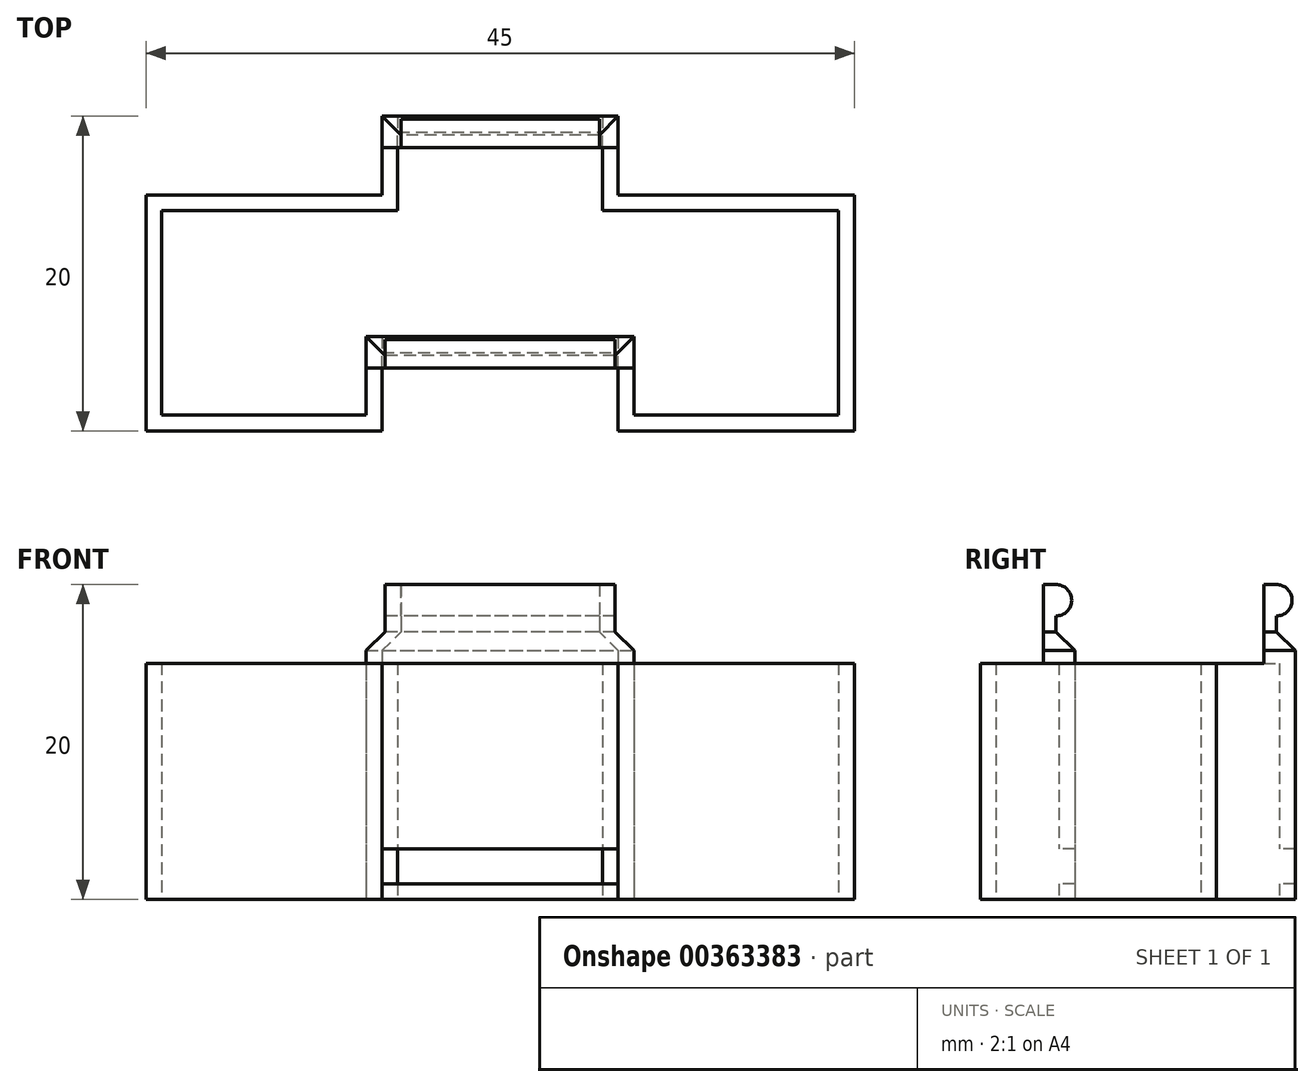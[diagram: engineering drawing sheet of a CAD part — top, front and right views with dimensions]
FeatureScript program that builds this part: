
annotation { "Feature Type Name" : "Feature", "Feature Type Description" : "" }
export const myFeature = defineFeature(function(context is Context, id is Id, definition is map)
    precondition{}
    {
        {
            assignVariable(context, id + "F0", {"name" : "Size", "anyValue" : 15});
        }
        {
            assignVariable(context, id + "F1", {"name" : "Thickness", "anyValue" : 1});
        }
        {
            var Q0;
            Q0=qCreatedBy(makeId("Top.planeOp"),FACE);
            var sketch = newSketch(context, id + "F2", { "sketchPlane" : qUnion([Q0])});
            skLineSegment(sketch, "E0.bottom", {"start": v(-24.33, 0) * mm, "end": v(-39.33, 0) * mm});
            skLineSegment(sketch, "E0.top", {"start": v(-24.33, 15) * mm, "end": v(-39.33, 15) * mm});
            skLineSegment(sketch, "E0.left", {"start": v(-24.33, 0) * mm, "end": v(-24.33, 15) * mm});
            skLineSegment(sketch, "E0.right", {"start": v(-39.33, 0) * mm, "end": v(-39.33, 15) * mm});
            skLineSegment(sketch, "E1.bottom", {"start": v(-9.33, 0) * mm, "end": v(5.67, 0) * mm});
            skLineSegment(sketch, "E1.top", {"start": v(-9.33, 15) * mm, "end": v(5.67, 15) * mm});
            skLineSegment(sketch, "E1.left", {"start": v(-9.33, 0) * mm, "end": v(-9.33, 15) * mm});
            skLineSegment(sketch, "E1.right", {"start": v(5.67, 0) * mm, "end": v(5.67, 15) * mm});
            skLineSegment(sketch, "E2.0", {"start": v(-38.33, 1) * mm, "end": v(-38.33, 14) * mm});
            skLineSegment(sketch, "E2.1", {"start": v(-25.33, 1) * mm, "end": v(-38.33, 1) * mm});
            skLineSegment(sketch, "E2.2", {"start": v(-25.33, 1) * mm, "end": v(-25.33, 14) * mm});
            skLineSegment(sketch, "E2.3", {"start": v(-25.33, 14) * mm, "end": v(-38.33, 14) * mm});
            skLineSegment(sketch, "E3.0", {"start": v(-8.33, 1) * mm, "end": v(-8.33, 14) * mm});
            skLineSegment(sketch, "E3.1", {"start": v(-8.33, 1) * mm, "end": v(4.67, 1) * mm});
            skLineSegment(sketch, "E3.2", {"start": v(4.67, 1) * mm, "end": v(4.67, 14) * mm});
            skLineSegment(sketch, "E3.3", {"start": v(-8.33, 14) * mm, "end": v(4.67, 14) * mm});
            skPoint(sketch, "E4.oppositeSnap0", {"position": v(-9.33, 7.5) * mm});
            skLineSegment(sketch, "E4.bottom", {"start": v(-24.33, 5) * mm, "end": v(-9.33, 5) * mm});
            skLineSegment(sketch, "E4.top", {"start": v(-24.33, 20) * mm, "end": v(-9.33, 20) * mm});
            skLineSegment(sketch, "E4.left", {"start": v(-24.33, 5) * mm, "end": v(-24.33, 20) * mm});
            skLineSegment(sketch, "E4.right", {"start": v(-9.33, 5) * mm, "end": v(-9.33, 20) * mm});
            skLineSegment(sketch, "E5.0", {"start": v(-23.33, 6) * mm, "end": v(-23.33, 19) * mm});
            skLineSegment(sketch, "E5.1", {"start": v(-23.33, 6) * mm, "end": v(-10.33, 6) * mm});
            skLineSegment(sketch, "E5.2", {"start": v(-10.33, 6) * mm, "end": v(-10.33, 19) * mm});
            skLineSegment(sketch, "E5.3", {"start": v(-23.33, 19) * mm, "end": v(-10.33, 19) * mm});
            skLineSegment(sketch, "E6", {"start": v(-25.33, 6) * mm, "end": v(-8.33, 6) * mm});
            skLineSegment(sketch, "E7", {"start": v(-25.33, 14) * mm, "end": v(-8.33, 14) * mm});
            skSolve(sketch);
        }
        {
            var Q0;
            Q0=makeQuery(id+"F2.imprint","IMPRINT",FACE,{"disambiguationData":[TD([[makeQuery(id+"F2.imprint","IMPRINT",EDGE,{"derivedFrom":sQuery(id+"F2.wireOp",EDGE,"E0.bottom")}),-1.0]])]});
            var Q1;
            {var subQ5=sQuery(id+"F2.wireOp",EDGE,"E4.bottom");Q1=makeQuery(id+"F2.imprint","IMPRINT",FACE,{"disambiguationData":[TD([[makeQuery(id+"F2.imprint","IMPRINT",EDGE,{"derivedFrom":subQ5}),1.0]])]});}
            var Q2;
            Q2=makeQuery(id+"F2.imprint","IMPRINT",FACE,{"disambiguationData":[TD([[makeQuery(id+"F2.imprint","IMPRINT",EDGE,{"derivedFrom":sQuery(id+"F2.wireOp",EDGE,"E1.bottom")}),1.0]])]});
            var Q3;
            {var subQ6=sQuery(id+"F2.wireOp",EDGE,"E4.top");Q3=makeQuery(id+"F2.imprint","IMPRINT",FACE,{"disambiguationData":[TD([[makeQuery(id+"F2.imprint","IMPRINT",EDGE,{"derivedFrom":subQ6}),-1.0]])]});}
            extrude(context, id + "F3", {"entities" : qUnion([Q0, Q1, Q2, Q3]), "depth" : (getVariable(context, 'Size')) * mm});
        }
        {
            var Q0;
            Q0=makeQuery(id+"F3.opExtrude","CAP_FACE",FACE,{"disambiguationData":[OSD([sQuery(id+"F2.wireOp",EDGE,"E0.bottom"),sQuery(id+"F2.wireOp",EDGE,"E0.top"),sQuery(id+"F2.wireOp",EDGE,"E0.left"),sQuery(id+"F2.wireOp",EDGE,"E0.right"),sQuery(id+"F2.wireOp",EDGE,"E1.bottom"),sQuery(id+"F2.wireOp",EDGE,"E1.top"),sQuery(id+"F2.wireOp",EDGE,"E1.left"),sQuery(id+"F2.wireOp",EDGE,"E1.right"),sQuery(id+"F2.wireOp",EDGE,"E2.0"),sQuery(id+"F2.wireOp",EDGE,"E2.1"),sQuery(id+"F2.wireOp",EDGE,"E2.2"),sQuery(id+"F2.wireOp",EDGE,"E2.3"),sQuery(id+"F2.wireOp",EDGE,"E3.0"),sQuery(id+"F2.wireOp",EDGE,"E3.1"),sQuery(id+"F2.wireOp",EDGE,"E3.2"),sQuery(id+"F2.wireOp",EDGE,"E3.3"),sQuery(id+"F2.wireOp",EDGE,"E4.bottom"),sQuery(id+"F2.wireOp",EDGE,"E4.top"),sQuery(id+"F2.wireOp",EDGE,"E4.left"),sQuery(id+"F2.wireOp",EDGE,"E4.right"),sQuery(id+"F2.wireOp",EDGE,"E5.0"),sQuery(id+"F2.wireOp",EDGE,"E5.2"),sQuery(id+"F2.wireOp",EDGE,"E5.3"),sQuery(id+"F2.wireOp",EDGE,"E6"),sQuery(id+"F2.wireOp",EDGE,"E7")])],"isStart":false});
            var sketch = newSketch(context, id + "F4", { "sketchPlane" : qUnion([Q0])});
            skLineSegment(sketch, "E8.bottom", {"start": v(-25.33, 6) * mm, "end": v(-8.33, 6) * mm});
            skLineSegment(sketch, "E8.top", {"start": v(-25.33, 4) * mm, "end": v(-8.33, 4) * mm});
            skLineSegment(sketch, "E8.left", {"start": v(-25.33, 6) * mm, "end": v(-25.33, 4) * mm});
            skLineSegment(sketch, "E8.right", {"start": v(-8.33, 6) * mm, "end": v(-8.33, 4) * mm});
            skLineSegment(sketch, "E9", {"start": v(-25.33, 5) * mm, "end": v(-8.33, 5) * mm});
            skLineSegment(sketch, "E10.bottom", {"start": v(-24.33, 20) * mm, "end": v(-9.33, 20) * mm});
            skLineSegment(sketch, "E10.top", {"start": v(-24.33, 18) * mm, "end": v(-9.33, 18) * mm});
            skLineSegment(sketch, "E10.left", {"start": v(-24.33, 20) * mm, "end": v(-24.33, 18) * mm});
            skLineSegment(sketch, "E10.right", {"start": v(-9.33, 20) * mm, "end": v(-9.33, 18) * mm});
            skLineSegment(sketch, "E11", {"start": v(-24.33, 19) * mm, "end": v(-9.33, 19) * mm});
            skSolve(sketch);
        }
        {
            var Q0;
            {var subQ5=sQuery(id+"F4.wireOp",EDGE,"E8.bottom");Q0=makeQuery(id+"F4.imprint","IMPRINT",FACE,{"disambiguationData":[TD([[makeQuery(id+"F4.imprint","IMPRINT",EDGE,{"derivedFrom":subQ5}),-1.0]])]});}
            var Q1;
            {var subQ3=makeQuery(id+"F3.opExtrude","CAP_EDGE",EDGE,{"disambiguationData":[OSD([sQuery(id+"F2.wireOp",EDGE,"E1.left")])],"isStart":false});var subQ5=sQuery(id+"F4.wireOp",EDGE,"E9");var subQ7=makeQuery(id+"F4.imprint","INTERSECT",VERTEX,{"derivedFrom":[subQ3,subQ5]});Q1=makeQuery(id+"F4.imprint","IMPRINT",FACE,{"disambiguationData":[TD([[makeQuery(id+"F4.imprint","IMPRINT",EDGE,{"disambiguationData":[TD([[subQ7,-1.0]])],"derivedFrom":subQ5}),-1.0]])]});}
            var Q2;
            {var subQ0=sQuery(id+"F4.wireOp",EDGE,"E8.top");var subQ1=makeQuery(id+"F3.opExtrude","CAP_EDGE",EDGE,{"disambiguationData":[OSD([sQuery(id+"F2.wireOp",EDGE,"E0.left")])],"isStart":false});var subQ2=makeQuery(id+"F4.imprint","INTERSECT",VERTEX,{"derivedFrom":[subQ1,subQ0]});Q2=makeQuery(id+"F4.imprint","IMPRINT",FACE,{"disambiguationData":[TD([[makeQuery(id+"F4.imprint","IMPRINT",EDGE,{"disambiguationData":[TD([[subQ2,-1.0]])],"derivedFrom":subQ0}),1.0]])]});}
            var Q3;
            {var subQ3=makeQuery(id+"F3.opExtrude","CAP_EDGE",EDGE,{"disambiguationData":[OSD([sQuery(id+"F2.wireOp",EDGE,"E0.left")])],"isStart":false});var subQ5=sQuery(id+"F4.wireOp",EDGE,"E9");var subQ7=makeQuery(id+"F4.imprint","INTERSECT",VERTEX,{"derivedFrom":[subQ3,subQ5]});Q3=makeQuery(id+"F4.imprint","IMPRINT",FACE,{"disambiguationData":[TD([[makeQuery(id+"F4.imprint","IMPRINT",EDGE,{"disambiguationData":[TD([[subQ7,1.0]])],"derivedFrom":subQ5}),-1.0]])]});}
            var Q4;
            {var subQ5=sQuery(id+"F4.wireOp",EDGE,"E10.bottom");Q4=makeQuery(id+"F4.imprint","IMPRINT",FACE,{"disambiguationData":[TD([[makeQuery(id+"F4.imprint","IMPRINT",EDGE,{"derivedFrom":subQ5}),-1.0]])]});}
            var Q5;
            {var subQ3=makeQuery(id+"F3.opExtrude","CAP_EDGE",EDGE,{"disambiguationData":[OSD([sQuery(id+"F2.wireOp",EDGE,"E5.0")])],"isStart":false});var subQ5=sQuery(id+"F4.wireOp",EDGE,"E11");var subQ6=makeQuery(id+"F4.imprint","INTERSECT",VERTEX,{"derivedFrom":[subQ3,subQ5]});Q5=makeQuery(id+"F4.imprint","IMPRINT",FACE,{"disambiguationData":[TD([[makeQuery(id+"F4.imprint","IMPRINT",EDGE,{"disambiguationData":[TD([[subQ6,1.0]])],"derivedFrom":subQ5}),-1.0]])]});}
            var Q6;
            {var subQ0=sQuery(id+"F4.wireOp",EDGE,"E10.top");var subQ1=makeQuery(id+"F3.opExtrude","CAP_EDGE",EDGE,{"disambiguationData":[OSD([sQuery(id+"F2.wireOp",EDGE,"E5.0")])],"isStart":false});var subQ2=makeQuery(id+"F4.imprint","INTERSECT",VERTEX,{"derivedFrom":[subQ1,subQ0]});Q6=makeQuery(id+"F4.imprint","IMPRINT",FACE,{"disambiguationData":[TD([[makeQuery(id+"F4.imprint","IMPRINT",EDGE,{"disambiguationData":[TD([[subQ2,-1.0]])],"derivedFrom":subQ0}),1.0]])]});}
            var Q7;
            {var subQ3=makeQuery(id+"F3.opExtrude","CAP_EDGE",EDGE,{"disambiguationData":[OSD([sQuery(id+"F2.wireOp",EDGE,"E5.2")])],"isStart":false});var subQ5=sQuery(id+"F4.wireOp",EDGE,"E11");var subQ6=makeQuery(id+"F4.imprint","INTERSECT",VERTEX,{"derivedFrom":[subQ3,subQ5]});Q7=makeQuery(id+"F4.imprint","IMPRINT",FACE,{"disambiguationData":[TD([[makeQuery(id+"F4.imprint","IMPRINT",EDGE,{"disambiguationData":[TD([[subQ6,-1.0]])],"derivedFrom":subQ5}),-1.0]])]});}
            extrude(context, id + "F5", {"entities" : qUnion([Q0, Q1, Q2, Q3, Q4, Q5, Q6, Q7]), "operationType" : NewBodyOperationType.ADD, "depth" : (getVariable(context, 'Thickness') * 2) * mm});
        }
        {
            var Q0;
            Q0=makeQuery(id+"F5.opExtrude","CAP_EDGE",EDGE,{"disambiguationData":[OSD([sQuery(id+"F4.wireOp",EDGE,"E8.bottom")])],"isStart":false});
            var Q1;
            Q1=makeQuery(id+"F5.opExtrude","CAP_EDGE",EDGE,{"disambiguationData":[OSD([sQuery(id+"F4.wireOp",EDGE,"E8.left")])],"isStart":false});
            var Q2;
            Q2=makeQuery(id+"F5.opExtrude","CAP_EDGE",EDGE,{"disambiguationData":[OSD([sQuery(id+"F4.wireOp",EDGE,"E8.right")])],"isStart":false});
            var Q3;
            Q3=makeQuery(id+"F5.opExtrude","CAP_EDGE",EDGE,{"disambiguationData":[OSD([sQuery(id+"F4.wireOp",EDGE,"E10.bottom")])],"isStart":false});
            var Q4;
            Q4=makeQuery(id+"F5.opExtrude","CAP_EDGE",EDGE,{"disambiguationData":[OSD([sQuery(id+"F4.wireOp",EDGE,"E10.left")])],"isStart":false});
            var Q5;
            Q5=makeQuery(id+"F5.opExtrude","CAP_EDGE",EDGE,{"disambiguationData":[OSD([sQuery(id+"F4.wireOp",EDGE,"E10.right")])],"isStart":false});
            chamfer(context, id + "F6", {"entities" : qUnion([Q0, Q1, Q2, Q3, Q4, Q5]), "width" : (getVariable(context, 'Thickness') + .2) * mm, "tangentPropagation" : true});
        }
        {
            var Q0;
            Q0=makeQuery(id+"F5.opExtrude","CAP_FACE",FACE,{"disambiguationData":[OSD([sQuery(id+"F4.wireOp",EDGE,"E8.bottom"),sQuery(id+"F4.wireOp",EDGE,"E8.top"),sQuery(id+"F4.wireOp",EDGE,"E8.left"),sQuery(id+"F4.wireOp",EDGE,"E8.right")])],"isStart":false});
            var Q1;
            Q1=makeQuery(id+"F5.opExtrude","CAP_FACE",FACE,{"disambiguationData":[OSD([sQuery(id+"F4.wireOp",EDGE,"E10.bottom"),sQuery(id+"F4.wireOp",EDGE,"E10.top"),sQuery(id+"F4.wireOp",EDGE,"E10.left"),sQuery(id+"F4.wireOp",EDGE,"E10.right")])],"isStart":false});
            extrude(context, id + "F7", {"entities" : qUnion([Q0, Q1]), "operationType" : NewBodyOperationType.ADD, "depth" : (getVariable(context, 'Size') / 3 - 2) * mm});
        }
        {
            var Q0;
            Q0=makeQuery(id+"F7.opExtrude","SWEPT_FACE",FACE,{"disambiguationData":[OSD([sQuery(id+"F4.wireOp",EDGE,"E8.bottom"),sQuery(id+"F4.wireOp",EDGE,"E8.top"),sQuery(id+"F4.wireOp",EDGE,"E8.left"),sQuery(id+"F4.wireOp",EDGE,"E8.right")])]});
            var sketch = newSketch(context, id + "F8", { "sketchPlane" : qUnion([Q0])});
            skLineSegment(sketch, "E12.bottom", {"start": v(9.53, 20) * mm, "end": v(24.13, 20) * mm});
            skLineSegment(sketch, "E12.top", {"start": v(9.53, 18) * mm, "end": v(24.13, 18) * mm});
            skLineSegment(sketch, "E12.left", {"start": v(9.53, 20) * mm, "end": v(9.53, 18) * mm});
            skLineSegment(sketch, "E12.right", {"start": v(24.13, 20) * mm, "end": v(24.13, 18) * mm});
            skSolve(sketch);
        }
        {
            var Q0;
            {var subQ0=sQuery(id+"F4.wireOp",EDGE,"E10.right");var subQ1=sQuery(id+"F4.wireOp",EDGE,"E10.left");var subQ2=sQuery(id+"F4.wireOp",EDGE,"E10.top");var subQ3=sQuery(id+"F4.wireOp",EDGE,"E10.bottom");Q0=makeQuery(id+"F7.opExtrude","SWEPT_FACE",FACE,{"disambiguationData":[OSD([subQ3,subQ2,subQ1,subQ0]),TDD([makeQuery(id+"F6.opChamfer","BLEND_EDGE",EDGE,{"blendedFrom":[makeQuery(id+"F5.opExtrude","CAP_EDGE",EDGE,{"disambiguationData":[OSD([subQ3])],"isStart":false}),makeQuery(id+"F5.opExtrude","CAP_FACE",FACE,{"disambiguationData":[OSD([subQ3,subQ2,subQ1,subQ0])],"isStart":false})],"blendedInto":[makeQuery(id+"F5.opExtrude","CAP_FACE",FACE,{"disambiguationData":[OSD([subQ3,subQ2,subQ1,subQ0])],"isStart":false})]})])]});}
            var sketch = newSketch(context, id + "F9", { "sketchPlane" : qUnion([Q0])});
            skLineSegment(sketch, "E13.bottom", {"start": v(10.53, 20) * mm, "end": v(23.13, 20) * mm});
            skLineSegment(sketch, "E13.top", {"start": v(10.53, 18) * mm, "end": v(23.13, 18) * mm});
            skLineSegment(sketch, "E13.left", {"start": v(10.53, 20) * mm, "end": v(10.53, 18) * mm});
            skLineSegment(sketch, "E13.right", {"start": v(23.13, 20) * mm, "end": v(23.13, 18) * mm});
            skSolve(sketch);
        }
        {
            var Q0;
            Q0=makeQuery(id+"F8.imprint","IMPRINT",FACE,{"disambiguationData":[TD([[makeQuery(id+"F8.imprint","IMPRINT",EDGE,{"derivedFrom":sQuery(id+"F8.wireOp",EDGE,"E12.bottom")}),-1.0]])]});
            var Q1;
            Q1=makeQuery(id+"F9.imprint","IMPRINT",FACE,{"disambiguationData":[TD([[makeQuery(id+"F9.imprint","IMPRINT",EDGE,{"derivedFrom":sQuery(id+"F9.wireOp",EDGE,"E13.bottom")}),-1.0]])]});
            extrude(context, id + "F10", {"entities" : qUnion([Q0, Q1]), "operationType" : NewBodyOperationType.ADD, "depth" : 1 * mm});
        }
        {
            var Q0;
            Q0=makeQuery(id+"F10.opExtrude","CAP_EDGE",EDGE,{"disambiguationData":[OSD([sQuery(id+"F8.wireOp",EDGE,"E12.bottom")])],"isStart":false});
            var Q1;
            Q1=makeQuery(id+"F10.opExtrude","CAP_EDGE",EDGE,{"disambiguationData":[OSD([sQuery(id+"F8.wireOp",EDGE,"E12.top")])],"isStart":false});
            var Q2;
            Q2=makeQuery(id+"F10.opExtrude","CAP_EDGE",EDGE,{"disambiguationData":[OSD([sQuery(id+"F9.wireOp",EDGE,"E13.bottom")])],"isStart":false});
            var Q3;
            Q3=makeQuery(id+"F10.opExtrude","CAP_EDGE",EDGE,{"disambiguationData":[OSD([sQuery(id+"F9.wireOp",EDGE,"E13.top")])],"isStart":false});
            fillet(context, id + "F11", {"entities" : qUnion([Q0, Q1, Q2, Q3]), "radius" : 1 * mm, "tangentPropagation" : true, "allowEdgeOverflow" : false});
        }
        {
            var Q0;
            Q0=makeQuery(id+"F3.opExtrude","SWEPT_FACE",FACE,{"disambiguationData":[OSD([sQuery(id+"F2.wireOp",EDGE,"E4.bottom")])]});
            var sketch = newSketch(context, id + "F12", { "sketchPlane" : qUnion([Q0])});
            skLineSegment(sketch, "E14.bottom", {"start": v(-24.33, 3.2) * mm, "end": v(-9.33, 3.2) * mm});
            skLineSegment(sketch, "E14.top", {"start": v(-24.33, 1) * mm, "end": v(-9.33, 1) * mm});
            skLineSegment(sketch, "E14.left", {"start": v(-24.33, 3.2) * mm, "end": v(-24.33, 1) * mm});
            skLineSegment(sketch, "E14.right", {"start": v(-9.33, 3.2) * mm, "end": v(-9.33, 1) * mm});
            skSolve(sketch);
        }
        {
            var Q0;
            Q0=makeQuery(id+"F3.opExtrude","SWEPT_FACE",FACE,{"disambiguationData":[OSD([sQuery(id+"F2.wireOp",EDGE,"E5.3")])]});
            var sketch = newSketch(context, id + "F13", { "sketchPlane" : qUnion([Q0])});
            skLineSegment(sketch, "E15.0.0", {"start": v(-24.33, 3.2) * mm, "end": v(-24.33, 1) * mm});
            skLineSegment(sketch, "E15.0.1", {"start": v(-24.33, 1) * mm, "end": v(-9.33, 1) * mm});
            skLineSegment(sketch, "E15.0.2", {"start": v(-9.33, 1) * mm, "end": v(-9.33, 3.2) * mm});
            skLineSegment(sketch, "E15.0.3", {"start": v(-9.33, 3.2) * mm, "end": v(-24.33, 3.2) * mm});
            skSolve(sketch);
        }
        {
            var Q0;
            Q0=makeQuery(id+"F12.imprint","IMPRINT",FACE,{"disambiguationData":[TD([[makeQuery(id+"F12.imprint","IMPRINT",EDGE,{"derivedFrom":sQuery(id+"F12.wireOp",EDGE,"E14.bottom")}),-1.0]])]});
            var Q1;
            {var subQ0=sQuery(id+"F13.wireOp",EDGE,"E15.0.1");var subQ1=sQuery(id+"F2.wireOp",EDGE,"E5.3");var subQ2=makeQuery(id+"F3.opExtrude","SWEPT_EDGE",EDGE,{"disambiguationData":[OSD([sQuery(id+"F2.wireOp",EDGE,"E5.0"),subQ1])]});var subQ3=makeQuery(id+"F13.imprint","INTERSECT",VERTEX,{"derivedFrom":[subQ2,subQ0]});Q1=makeQuery(id+"F13.imprint","IMPRINT",FACE,{"disambiguationData":[TD([[makeQuery(id+"F13.imprint","IMPRINT",EDGE,{"disambiguationData":[TD([[subQ3,-1.0]])],"derivedFrom":subQ0}),1.0]])]});}
            extrude(context, id + "F14", {"entities" : qUnion([Q0, Q1]), "operationType" : NewBodyOperationType.REMOVE, "endBound" : BoundingType.UP_TO_NEXT, "oppositeDirection" : true, "depth" : 25 * mm});
        }
    });
